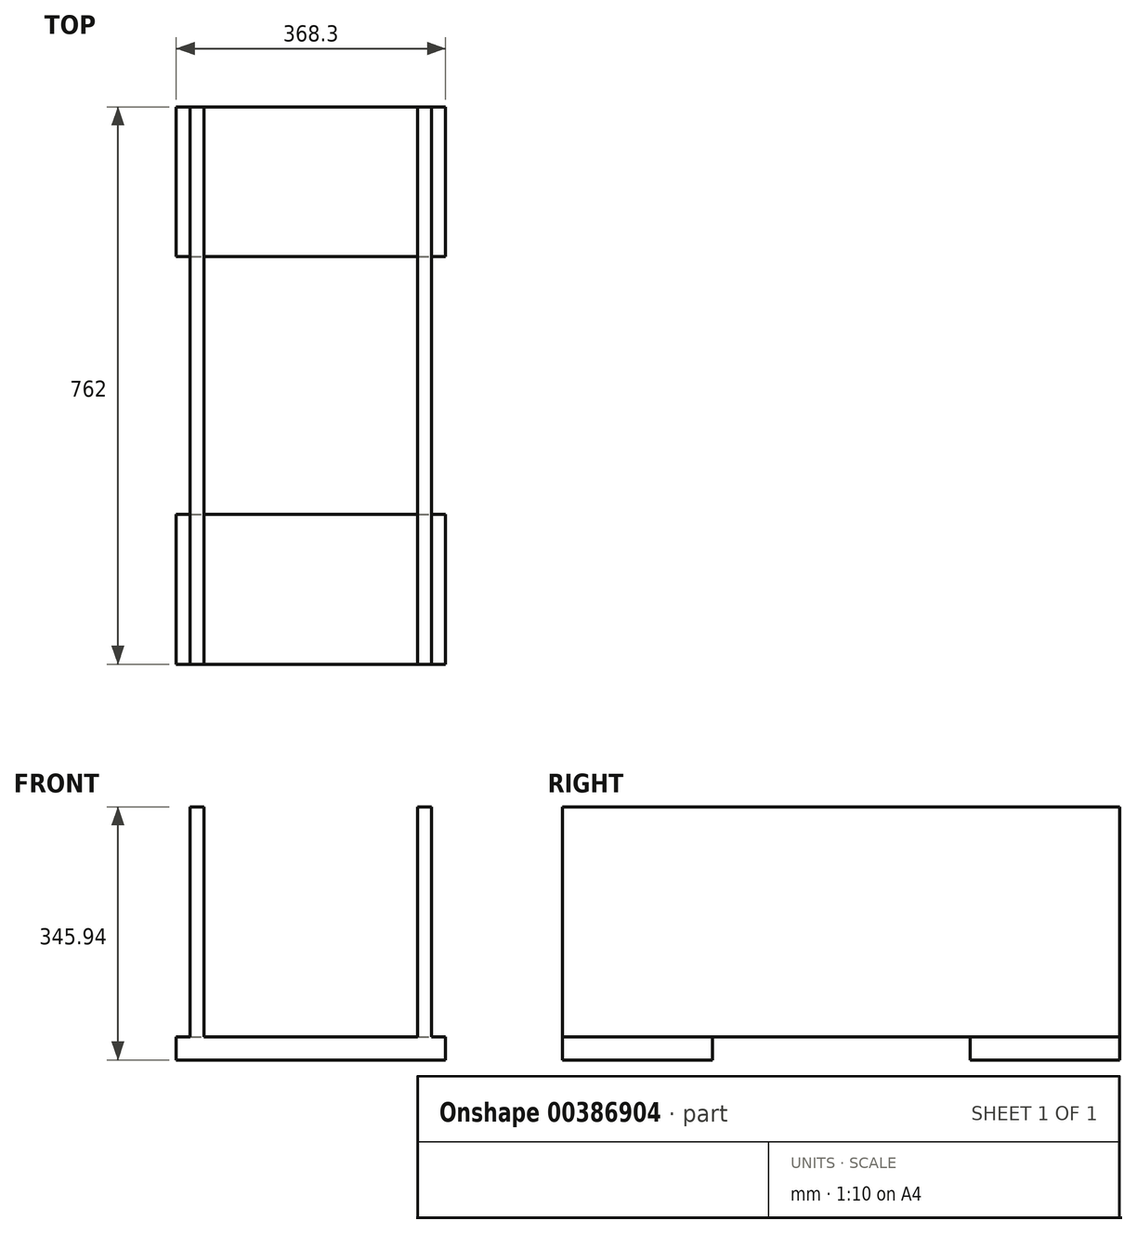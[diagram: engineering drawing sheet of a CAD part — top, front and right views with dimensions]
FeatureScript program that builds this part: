
annotation { "Feature Type Name" : "Feature", "Feature Type Description" : "" }
export const myFeature = defineFeature(function(context is Context, id is Id, definition is map)
    precondition{}
    {
        {
            var Q0;
            Q0=qCreatedBy(makeId("Front.planeOp"),FACE);
            var sketch = newSketch(context, id + "F0", { "sketchPlane" : qUnion([Q0])});
            skLineSegment(sketch, "E0", {"start": v(0, 0) * mm, "end": v(184.15, 0) * mm});
            skLineSegment(sketch, "E1", {"start": v(184.15, 0) * mm, "end": v(184.15, 31.75) * mm});
            skLineSegment(sketch, "E2", {"start": v(184.15, 31.75) * mm, "end": v(-184.15, 31.75) * mm});
            skLineSegment(sketch, "E3", {"start": v(-184.15, 31.75) * mm, "end": v(-184.15, 0) * mm});
            skLineSegment(sketch, "E4", {"start": v(-184.15, 0) * mm, "end": v(0, 0) * mm});
            skLineSegment(sketch, "E5.bottom", {"start": v(-165.1, 31.75) * mm, "end": v(-146.05, 31.75) * mm});
            skLineSegment(sketch, "E5.top", {"start": v(-165.1, 345.94) * mm, "end": v(-146.05, 345.94) * mm});
            skLineSegment(sketch, "E5.left", {"start": v(-165.1, 31.75) * mm, "end": v(-165.1, 345.94) * mm});
            skLineSegment(sketch, "E5.right", {"start": v(-146.05, 31.75) * mm, "end": v(-146.05, 345.94) * mm});
            skLineSegment(sketch, "E6.bottom", {"start": v(146.05, 31.75) * mm, "end": v(165.1, 31.75) * mm});
            skLineSegment(sketch, "E6.top", {"start": v(146.05, 345.94) * mm, "end": v(165.1, 345.94) * mm});
            skLineSegment(sketch, "E6.left", {"start": v(146.05, 31.75) * mm, "end": v(146.05, 345.94) * mm});
            skLineSegment(sketch, "E6.right", {"start": v(165.1, 31.75) * mm, "end": v(165.1, 345.94) * mm});
            skSolve(sketch);
        }
        {
            var Q0;
            Q0 = qSketchRegion(id + "F0", true);
            extrude(context, id + "F1", {"entities" : qUnion([Q0]), "depth" : 762 * mm, "offsetDistance" : 25 * mm, "symmetric" : true});
        }
        {
            var Q0;
            Q0=qCreatedBy(makeId("Right.planeOp"),FACE);
            var sketch = newSketch(context, id + "F2", { "sketchPlane" : qUnion([Q0])});
            skLineSegment(sketch, "E7.bottom", {"start": v(176.34, 0) * mm, "end": v(-176.34, 0) * mm});
            skLineSegment(sketch, "E7.top", {"start": v(176.34, 31.75) * mm, "end": v(-176.34, 31.75) * mm});
            skLineSegment(sketch, "E7.left", {"start": v(176.34, 0) * mm, "end": v(176.34, 31.75) * mm});
            skLineSegment(sketch, "E7.right", {"start": v(-176.34, 0) * mm, "end": v(-176.34, 31.75) * mm});
            skSolve(sketch);
        }
        {
            var Q0;
            Q0 = qSketchRegion(id + "F2", true);
            extrude(context, id + "F3", {"entities" : qUnion([Q0]), "operationType" : NewBodyOperationType.REMOVE, "oppositeDirection" : true, "depth" : 368.3 * mm, "offsetDistance" : 25 * mm, "symmetric" : true});
        }
    });
